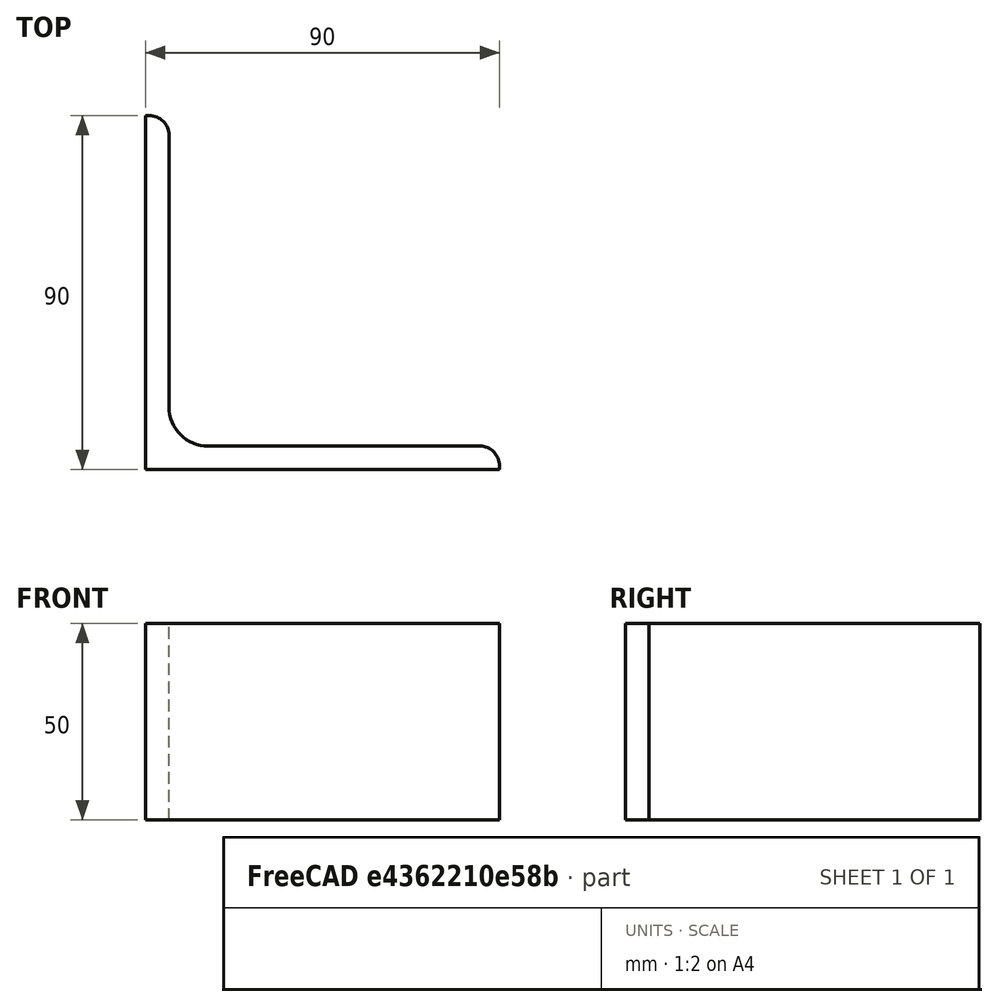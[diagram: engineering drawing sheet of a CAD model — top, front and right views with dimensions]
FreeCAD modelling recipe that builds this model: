
FCSTD DOCUMENT  (FreeCAD 0.15R4671 (Git))
Label: Angle Bar L90x90x6 EN10056 S235JR
License: All rights reserved
LicenseURL: http://en.wikipedia.org/wiki/All_rights_reserved
objects: Sketcher::SketchObject×1, Part::Extrusion×1
note: 2 computed .brp shape members not serialized (recipe doc carries the construction recipe); baked Part::Feature solids carry a one-line shape summary decoded from their .brp

FEATURE [Sketcher::SketchObject] Sketch
  sketch-geometry (9):
    g0: LineSegment StartX=0 StartY=0 StartZ=0 EndX=90 EndY=0 EndZ=0
    g1: LineSegment StartX=90 StartY=0 StartZ=0 EndX=90 EndY=1 EndZ=0
    g2: LineSegment StartX=85 StartY=6 StartZ=0 EndX=16 EndY=6 EndZ=0
    g3: LineSegment StartX=0 StartY=0 StartZ=0 EndX=0 EndY=90 EndZ=0
    g4: LineSegment StartX=0 StartY=90 StartZ=0 EndX=1 EndY=90 EndZ=0
    g5: LineSegment StartX=6 StartY=85 StartZ=0 EndX=6 EndY=16 EndZ=0
    g6: ArcOfCircle CenterX=16 CenterY=16 CenterZ=0 NormalX=0 NormalY=0 NormalZ=1 Radius=10 StartAngle=3.14159 EndAngle=4.71239
    g7: ArcOfCircle CenterX=1 CenterY=85 CenterZ=0 NormalX=0 NormalY=0 NormalZ=1 Radius=5 StartAngle=0 EndAngle=1.5708
    g8: ArcOfCircle CenterX=85 CenterY=1 CenterZ=0 NormalX=0 NormalY=0 NormalZ=1 Radius=5 StartAngle=0 EndAngle=1.5708
  constraints (23):
    c: Coincident(g0,g-1)
    c: Horizontal(g0)
    c: Coincident(g1,g0)
    c: Vertical(g1)
    c: Horizontal(g2)
    c: Coincident(g3,g-1)
    c: Vertical(g3)
    c: Coincident(g4,g3)
    c: Horizontal(g4)
    c: Vertical(g5)
    c: Tangent(g5,g6) = -1.5708
    c: Tangent(g2,g6) = 1.5708
    c: Tangent(g4,g7) = 1.5708
    c: Tangent(g5,g7) = 1.5708
    c: Tangent(g2,g8) = -1.5708
    c: Tangent(g1,g8) = -1.5708
    c: DistanceX(g0) = 90
    c: DistanceY(g3) = 90
    c: DistanceY(g0,g2) = 6
    c: DistanceX(g3,g5) = 6
    c: Radius(g6) = 10
    c: Radius(g8) = 5
    c: Radius(g7) = 5
FEATURE [Part::Extrusion] Extrude  label="Angle Bar L90x90x6 EN10056 S235JR"
  Base = -> Sketch
  Dir = (0,0,50)
  Solid = true
